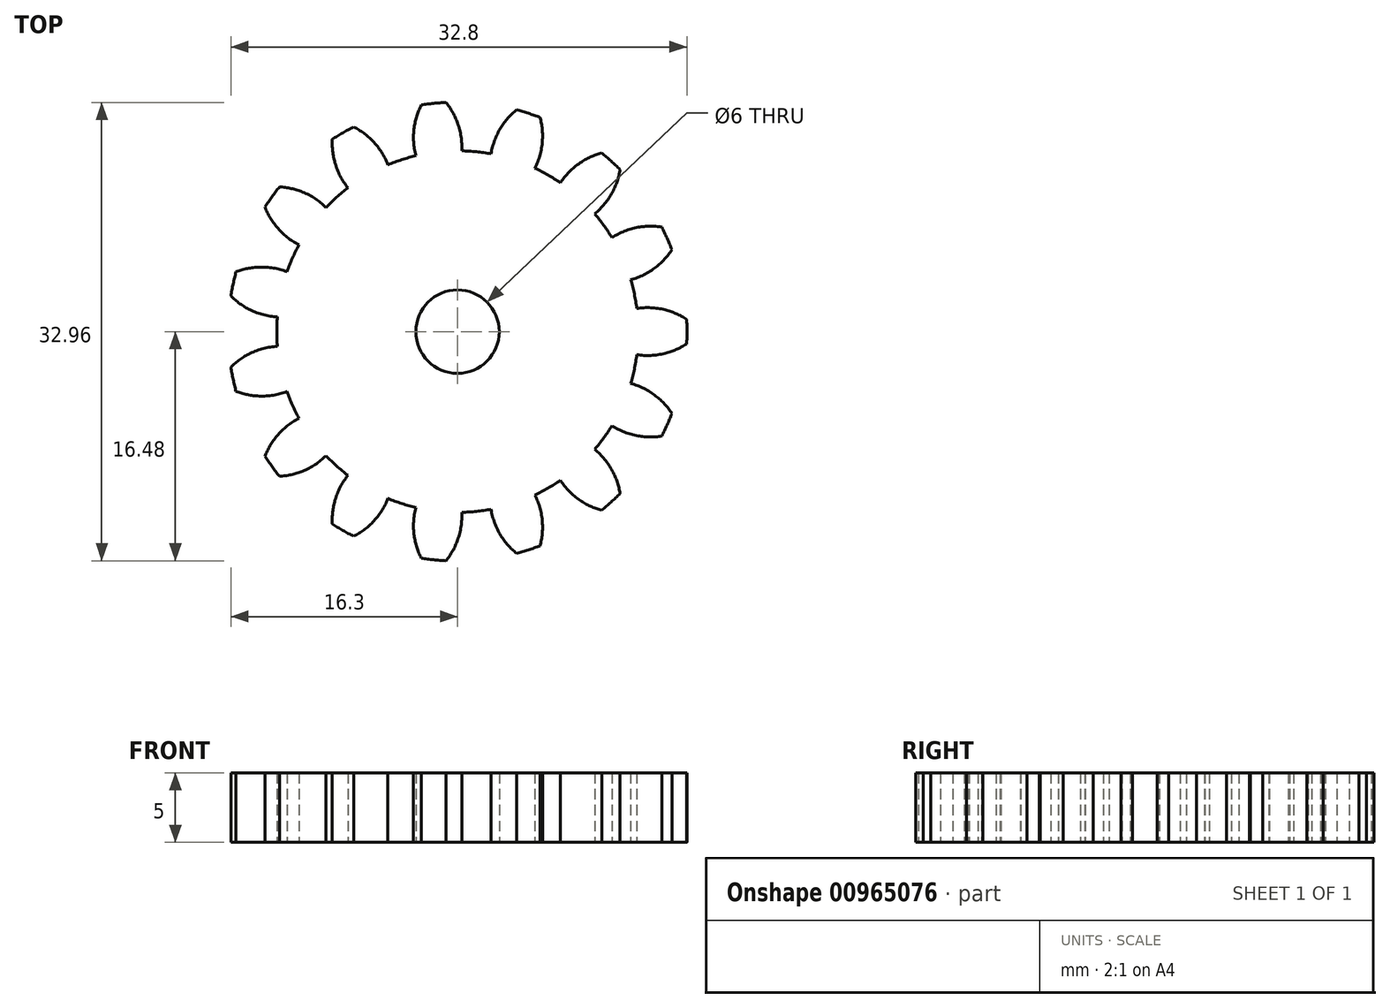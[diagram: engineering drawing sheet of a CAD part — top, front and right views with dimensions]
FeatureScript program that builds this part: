
annotation { "Feature Type Name" : "Feature", "Feature Type Description" : "" }
export const myFeature = defineFeature(function(context is Context, id is Id, definition is map)
    precondition{}
    {
        {
            var Q0;
            Q0=qCreatedBy(makeId("Top.planeOp"),FACE);
            var sketch = newSketch(context, id + "F0", { "sketchPlane" : qUnion([Q0])});
            skCircle(sketch, "E0", {"center": v(0, 0) * mm, "radius": 13 * mm});
            skCircle(sketch, "E1", {"center": v(0, 0) * mm, "radius": 15 * mm, "construction": true});
            skCircle(sketch, "E2", {"center": v(0, 0) * mm, "radius": 16.5 * mm, "construction": true});
            skLineSegment(sketch, "E3", {"start": v(0, 0) * mm, "end": v(0, 27.2) * mm, "construction": true});
            skLineSegment(sketch, "E4", {"start": v(0, 0) * mm, "end": v(-2.84, 27.02) * mm, "construction": true});
            skLineSegment(sketch, "E5", {"start": v(0, 15) * mm, "end": v(-22.3, 15) * mm, "construction": true});
            skLineSegment(sketch, "E6", {"start": v(0, 15) * mm, "end": v(-23.04, 6.61) * mm, "construction": true});
            skLineSegment(sketch, "E7", {"start": v(0, 0) * mm, "end": v(-4.82, 13.25) * mm, "construction": true});
            skCircle(sketch, "E8", {"center": v(0, 0) * mm, "radius": 14.1 * mm, "construction": true});
            skCircle(sketch, "E9", {"center": v(0, 15) * mm, "radius": 5.13 * mm, "construction": true});
            skCircle(sketch, "E10", {"center": v(-4.82, 13.25) * mm, "radius": 5.13 * mm, "construction": true});
            skArc(sketch, "E11", {"start": v(0, 15) * mm, "mid": v(-0.36, 15.77) * mm, "end": v(-0.84, 16.48) * mm});
            skArc(sketch, "E12", {"start": v(0.3, 13) * mm, "mid": v(0.25, 14.01) * mm, "end": v(0, 15) * mm});
            skArc(sketch, "E13.MirrorCS", {"start": v(-3.12, 14.67) * mm, "mid": v(-2.93, 15.5) * mm, "end": v(-2.6, 16.3) * mm});
            skArc(sketch, "E14.MirrorCS", {"start": v(-3, 12.65) * mm, "mid": v(-3.16, 13.65) * mm, "end": v(-3.12, 14.67) * mm});
            skArc(sketch, "E15", {"start": v(-0.84, 16.48) * mm, "mid": v(-1.72, 16.4) * mm, "end": v(-2.6, 16.3) * mm});
            skCircle(sketch, "E16", {"center": v(0, 0) * mm, "radius": 3 * mm});
            skSolve(sketch);
        }
        {
            var Q0;
            {var subQ0=sQuery(id+"F0.wireOp",EDGE,"E0");var subQ1=makeQuery(id+"F0.imprint","INTERSECT",VERTEX,{"derivedFrom":[subQ0,sQuery(id+"F0.wireOp",EDGE,"E12")]});Q0=makeQuery(id+"F0.imprint","IMPRINT",FACE,{"disambiguationData":[TD([[makeQuery(id+"F0.imprint","IMPRINT",EDGE,{"disambiguationData":[TD([[subQ1,-1.0]])],"derivedFrom":subQ0}),1.0]])]});}
            var Q1;
            Q1=makeQuery(id+"F0.imprint","IMPRINT",FACE,{"disambiguationData":[TD([[makeQuery(id+"F0.imprint","IMPRINT",EDGE,{"derivedFrom":sQuery(id+"F0.wireOp",EDGE,"E11")}),1.0]])]});
            extrude(context, id + "F1", {"entities" : qUnion([Q0, Q1]), "depth" : 5 * mm, "offsetDistance" : 25 * mm});
        }
        {
            var Q0;
            Q0=makeQuery(id+"F1.opExtrude","SWEPT_FACE",FACE,{"disambiguationData":[OSD([sQuery(id+"F0.wireOp",EDGE,"E11")])]});
            var Q1;
            Q1=makeQuery(id+"F1.opExtrude","SWEPT_FACE",FACE,{"disambiguationData":[OSD([sQuery(id+"F0.wireOp",EDGE,"E15")])]});
            var Q2;
            Q2=makeQuery(id+"F1.opExtrude","SWEPT_FACE",FACE,{"disambiguationData":[OSD([sQuery(id+"F0.wireOp",EDGE,"E12")])]});
            var Q3;
            Q3=makeQuery(id+"F1.opExtrude","SWEPT_FACE",FACE,{"disambiguationData":[OSD([sQuery(id+"F0.wireOp",EDGE,"E13.MirrorCS")])]});
            var Q4;
            Q4=makeQuery(id+"F1.opExtrude","SWEPT_FACE",FACE,{"disambiguationData":[OSD([sQuery(id+"F0.wireOp",EDGE,"E14.MirrorCS")])]});
            var Q5;
            Q5=makeQuery(id+"F1.opExtrude","SWEPT_FACE",FACE,{"disambiguationData":[OSD([sQuery(id+"F0.wireOp",EDGE,"E0")])]});
            circularPattern(context, id + "F2", {"patternType" : PatternType.FACE, "faces" : qUnion([Q0, Q1, Q2, Q3, Q4]), "axis" : qUnion([Q5]), "angle" : 360 * degree, "instanceCount" : 15, "equalSpace" : true});
        }
    });
